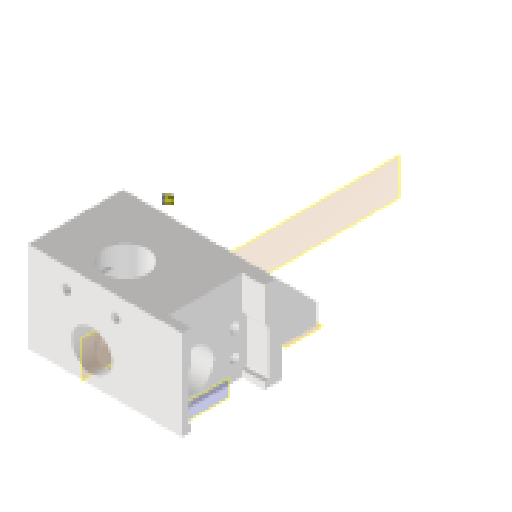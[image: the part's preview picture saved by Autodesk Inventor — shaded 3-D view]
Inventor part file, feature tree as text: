
AUTODESK INVENTOR PART (.ipt)
format: ipt  version: 2025.3 (Build 293356000, 356)  size: 477,184 bytes
history: native  units: mm
features: extrude x17, sketch x15, reference x15, projected_geometry x13, plane x10, other x5, chamfer x1
ambient origin geometry x8: Origin, YZ Plane, XZ Plane, XY Plane, X Axis, Y Axis, Z Axis, Center Point
bodies: Volumenkörper2 (feature_tree)
feature tree (76):
  plane  "Arbeitsebene6"
  extrude  "Extrusion12"  Depth=0.5mm
  extrude  "Extrusion13"  Depth=12.0mm
  plane  "Arbeitsebene7"
  plane  "Arbeitsebene8"
  plane  "Arbeitsebene9"
  plane  "Arbeitsebene10"
  sketch  "Skizze21"  dims[d76=35.97mm d77=0.0mm d87=0.5mm]
  plane  "Arbeitsebene11"
  extrude  "Extrusion18"  Depth=0.5mm
  plane  "Arbeitsebene12"
  extrude  "Extrusion22"  TaperAngle=0.0deg  [1 undecoded]
  extrude  "Extrusion23"  Depth=0.5mm
  extrude  "Extrusion27"  TaperAngle=0.0deg  [1 undecoded]
  sketch  "Skizze31"  dims[d107=12.0mm d108=0.0mm d109=0.0mm d110=0.0mm]
  plane  "Arbeitsebene13"
  extrude  "Extrusion28"  Depth=10.0mm
  extrude  "Extrusion29"  Depth=10.0mm TaperAngle=0.0deg
  sketch  "Skizze33"  dims[d111=10.0mm d112=0.0mm d113=0.1mm]
  plane  "Arbeitsebene14"
  extrude  "Extrusion30"  Depth=6.0mm
  sketch  "Skizze35"  dims[d114=0.1mm d116=10.0mm d117=0.0mm]
  plane  "Arbeitsebene15"
  extrude  "Extrusion32"  Depth=2.0mm
  extrude  "Extrusion33"  Depth=2.0mm
  extrude  "Extrusion34"  Depth=10.0mm TaperAngle=0.0deg
  extrude  "Extrusion35"  Depth=8.0mm TaperAngle=0.0deg
  extrude  "Extrusion36"  TaperAngle=0.0deg  [1 undecoded]
  extrude  "Extrusion37"  Depth=10.0mm TaperAngle=0.0deg
  extrude  "Extrusion38"  Depth=10.0mm TaperAngle=0.0deg
  extrude  "Extrusion39"  Depth=10.0mm TaperAngle=0.0deg
  chamfer  "Chamfer3"  Distance=2.8mm
  sketch  "Skizze13"  dims[d58=8.0mm d59=0.0mm d60=0.5mm]
  reference  "Referenz11"
  reference  "Referenz12"
  reference  "Referenz13"
  reference  "Referenz14"
  sketch  "Skizze16"  dims[d62=8.0mm d63=0.0mm d75=12.0mm]
  projected_geometry  "Projizierte Kontur9"
  reference  "Referenz15"
  reference  "Referenz25"
  reference  "Referenz26"
  reference  "Referenz27"
  sketch  "Skizze26"  dims[d88=10.0mm d89=0.0mm d90=0.0mm d91=0.0mm]
  sketch  "Skizze30"  dims[d93=20.0mm d94=0.5mm]
  reference  "Referenz30"
  reference  "Referenz31"
  reference  "Referenz32"
  reference  "Referenz33"
  reference  "Referenz34"
  reference  "Referenz35"
  reference  "Referenz36"
  projected_geometry  "Projizierte Kontur16"
  projected_geometry  "Projizierte Kontur17"
  sketch  "Skizze36"  dims[d120=6.0mm d121=9.5mm]
  projected_geometry  "Projizierte Kontur18"
  sketch  "Skizze37"  dims[d122=9.5mm d123=2.0mm]
  projected_geometry  "Projizierte Kontur19"
  projected_geometry  "Projizierte Kontur20"
  sketch  "Skizze38"  dims[d124=2.0mm d125=2.0mm]
  projected_geometry  "Projizierte Kontur21"
  sketch  "Sketch39"  dims[d126=2.5mm d127=10.0mm d128=0.0mm]
  projected_geometry  "Projected Loop22"
  sketch  "Sketch40"  dims[d129=12.0mm d130=8.0mm d131=0.0mm]
  projected_geometry  "Projected Loop23"
  sketch  "Sketch41"  dims[d132=12.8mm d133=0.0mm d134=0.0mm]
  projected_geometry  "Projected Loop24"
  sketch  "Sketch42"  dims[d135=2.8mm d136=8.0mm d137=0.0mm d138=10.0mm d139=0.0mm d140=10.0mm d141=0.0mm d142=2.8mm d143=2.8mm d144=10.0mm d145=0.0mm d146=2.0mm d147=0.0mm d148=12.0mm d149=2.0mm d150=45.0deg d15=0.5mm d16=0.872665mm d17=0.5mm d18=0.872665mm]
  projected_geometry  "Projected Loop25"
  projected_geometry  "Projected Loop26"
  projected_geometry  "Projected Loop27"
  other  "Assemlby_lightsheet_generator_passive_v2.iam"
  other  "30_Scanlens_Laseradaper_lid_v1:1"
  other  "00_SMAConnector_fiber copy:1"
  other  "30_Lightsheet_generator_passive_lid_v1:1"
  other  "30_Laser_to_M12Adapter:1"
note: 3 required parameter values undecoded (feature->parameter linkage not recoverable at this tier; creation-order binding heuristic only, values carry confidence <= 0.55)
